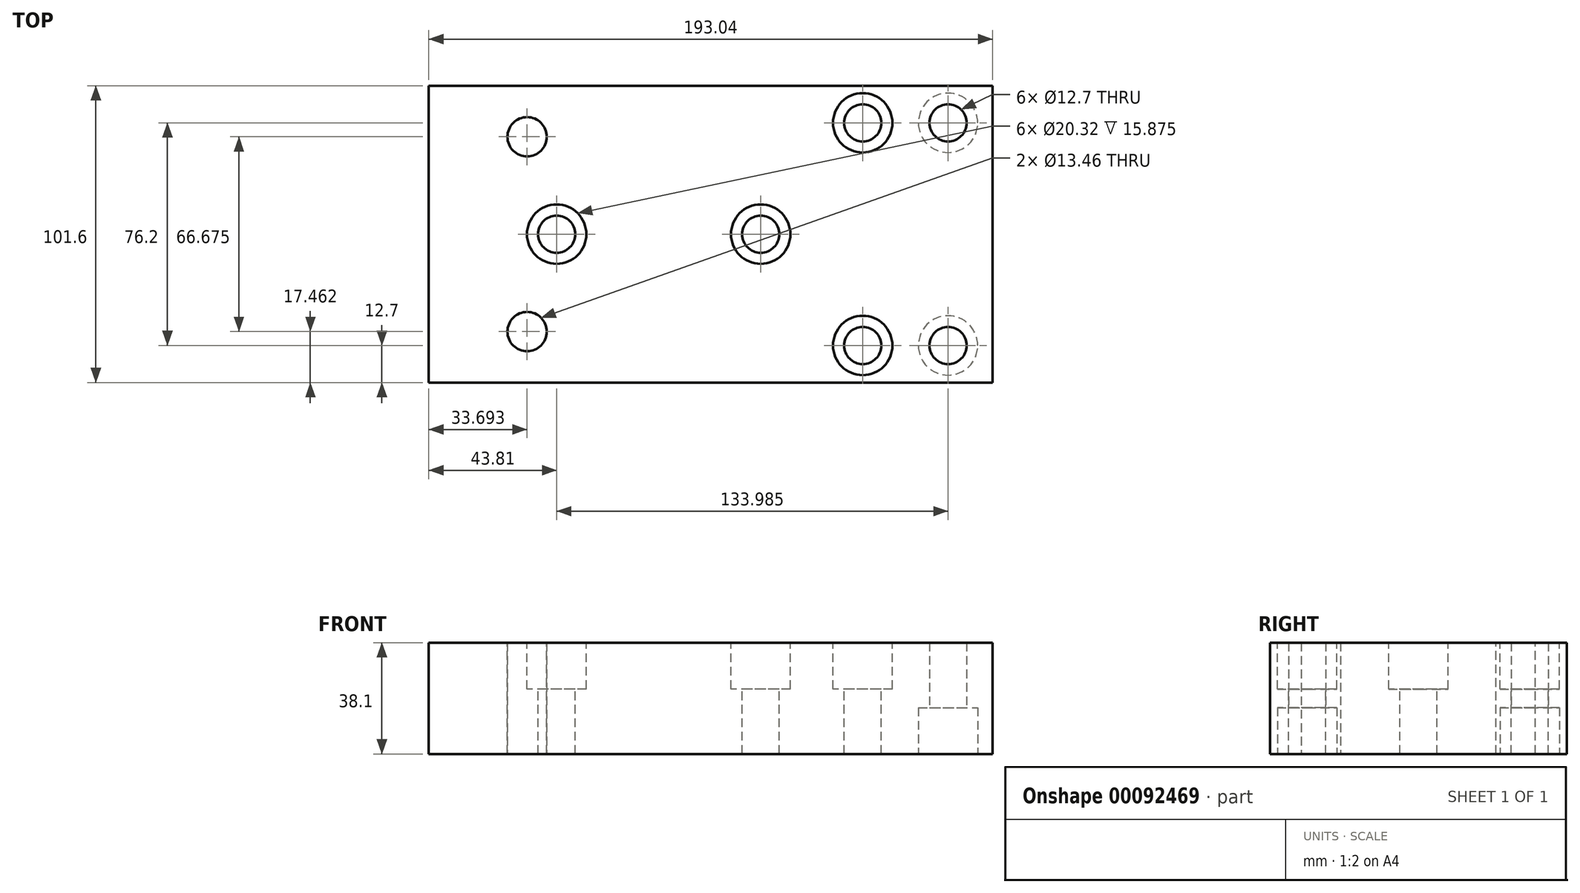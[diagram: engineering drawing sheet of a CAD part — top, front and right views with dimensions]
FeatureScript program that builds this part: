
annotation { "Feature Type Name" : "Feature", "Feature Type Description" : "" }
export const myFeature = defineFeature(function(context is Context, id is Id, definition is map)
    precondition{}
    {
        {
            var Q0;
            Q0=qCreatedBy(makeId("Top.planeOp"),FACE);
            var sketch = newSketch(context, id + "F0", { "sketchPlane" : qUnion([Q0])});
            skCircle(sketch, "E0", {"center": v(685.93, -42.2) * mm, "radius": 6.73 * mm});
            skCircle(sketch, "E1", {"center": v(685.93, 24.48) * mm, "radius": 6.73 * mm});
            skLineSegment(sketch, "E2", {"start": v(845.28, 41.94) * mm, "end": v(652.24, 41.94) * mm});
            skCircle(sketch, "E3", {"center": v(830.04, -46.96) * mm, "radius": 6.53 * mm});
            skCircle(sketch, "E4", {"center": v(830.04, 29.24) * mm, "radius": 6.53 * mm});
            skLineSegment(sketch, "E5", {"start": v(652.24, -59.66) * mm, "end": v(652.24, 41.94) * mm});
            skCircle(sketch, "E6", {"center": v(800.83, 29.24) * mm, "radius": 6.35 * mm});
            skCircle(sketch, "E7", {"center": v(800.83, -46.96) * mm, "radius": 6.35 * mm});
            skCircle(sketch, "E8", {"center": v(696.05, -8.86) * mm, "radius": 6.35 * mm});
            skCircle(sketch, "E9", {"center": v(765.9, -8.86) * mm, "radius": 6.35 * mm});
            skCircle(sketch, "E10", {"center": v(696.05, -8.86) * mm, "radius": 10.16 * mm});
            skCircle(sketch, "E11", {"center": v(765.9, -8.86) * mm, "radius": 10.16 * mm});
            skCircle(sketch, "E12", {"center": v(800.83, 29.24) * mm, "radius": 10.16 * mm});
            skCircle(sketch, "E13", {"center": v(800.83, -46.96) * mm, "radius": 10.16 * mm});
            skCircle(sketch, "E14", {"center": v(830.04, 29.24) * mm, "radius": 10.16 * mm});
            skCircle(sketch, "E15", {"center": v(830.04, -46.96) * mm, "radius": 10.16 * mm});
            skCircle(sketch, "E16", {"center": v(685.93, -191.42) * mm, "radius": 6.73 * mm});
            skCircle(sketch, "E17", {"center": v(685.93, -258.1) * mm, "radius": 6.73 * mm});
            skLineSegment(sketch, "E18", {"start": v(845.28, -97.76) * mm, "end": v(845.28, -135.86) * mm});
            skLineSegment(sketch, "E19", {"start": v(845.28, -275.56) * mm, "end": v(652.24, -275.56) * mm});
            skLineSegment(sketch, "E20", {"start": v(845.28, -173.96) * mm, "end": v(652.24, -173.96) * mm});
            skCircle(sketch, "E21", {"center": v(830.04, -186.66) * mm, "radius": 6.53 * mm});
            skCircle(sketch, "E22", {"center": v(830.04, -262.86) * mm, "radius": 6.53 * mm});
            skCircle(sketch, "E23", {"center": v(800.83, -262.86) * mm, "radius": 6.35 * mm});
            skCircle(sketch, "E24", {"center": v(800.83, -186.66) * mm, "radius": 6.35 * mm});
            skCircle(sketch, "E25", {"center": v(696.05, -224.76) * mm, "radius": 6.35 * mm});
            skCircle(sketch, "E26", {"center": v(765.9, -224.76) * mm, "radius": 6.35 * mm});
            skCircle(sketch, "E27", {"center": v(800.83, -262.86) * mm, "radius": 10.16 * mm});
            skCircle(sketch, "E28", {"center": v(800.83, -186.66) * mm, "radius": 10.16 * mm});
            skCircle(sketch, "E29", {"center": v(765.9, -224.76) * mm, "radius": 10.16 * mm});
            skCircle(sketch, "E30", {"center": v(696.05, -224.76) * mm, "radius": 10.16 * mm});
            skCircle(sketch, "E31", {"center": v(830.04, -186.66) * mm, "radius": 10.16 * mm});
            skCircle(sketch, "E32", {"center": v(830.04, -262.86) * mm, "radius": 10.16 * mm});
            skLineSegment(sketch, "E33", {"start": v(845.28, -173.96) * mm, "end": v(845.28, -275.56) * mm});
            skLineSegment(sketch, "E34", {"start": v(652.24, -97.76) * mm, "end": v(845.28, -97.76) * mm});
            skLineSegment(sketch, "E35", {"start": v(692.66, -97.76) * mm, "end": v(692.66, -135.86) * mm});
            skLineSegment(sketch, "E36", {"start": v(836.64, -97.76) * mm, "end": v(836.64, -121.57) * mm});
            skLineSegment(sketch, "E37", {"start": v(823.43, -121.57) * mm, "end": v(823.43, -97.76) * mm});
            skLineSegment(sketch, "E38", {"start": v(819.88, -135.86) * mm, "end": v(819.88, -121.57) * mm});
            skLineSegment(sketch, "E39", {"start": v(840.2, -121.57) * mm, "end": v(840.2, -135.86) * mm});
            skLineSegment(sketch, "E40", {"start": v(819.88, -121.57) * mm, "end": v(823.43, -121.57) * mm});
            skLineSegment(sketch, "E41", {"start": v(823.43, -121.57) * mm, "end": v(830.04, -121.57) * mm});
            skLineSegment(sketch, "E42", {"start": v(830.04, -121.57) * mm, "end": v(836.64, -121.57) * mm});
            skLineSegment(sketch, "E43", {"start": v(836.64, -121.57) * mm, "end": v(840.2, -121.57) * mm});
            skLineSegment(sketch, "E44", {"start": v(679.2, -97.76) * mm, "end": v(679.2, -135.86) * mm});
            skLineSegment(sketch, "E45", {"start": v(790.67, -112.05) * mm, "end": v(790.67, -97.76) * mm});
            skLineSegment(sketch, "E46", {"start": v(790.67, -112.05) * mm, "end": v(810.99, -112.05) * mm});
            skLineSegment(sketch, "E47", {"start": v(794.48, -135.86) * mm, "end": v(794.48, -112.05) * mm});
            skLineSegment(sketch, "E48", {"start": v(807.18, -112.05) * mm, "end": v(807.18, -135.86) * mm});
            skLineSegment(sketch, "E49", {"start": v(810.99, -97.76) * mm, "end": v(810.99, -112.05) * mm});
            skLineSegment(sketch, "E50", {"start": v(755.74, -112.05) * mm, "end": v(755.74, -97.76) * mm});
            skLineSegment(sketch, "E51", {"start": v(755.74, -112.05) * mm, "end": v(776.06, -112.05) * mm});
            skLineSegment(sketch, "E52", {"start": v(759.55, -135.86) * mm, "end": v(759.55, -112.05) * mm});
            skLineSegment(sketch, "E53", {"start": v(772.25, -112.05) * mm, "end": v(772.25, -135.86) * mm});
            skLineSegment(sketch, "E54", {"start": v(776.06, -97.76) * mm, "end": v(776.06, -112.05) * mm});
            skLineSegment(sketch, "E55", {"start": v(759.55, -173.96) * mm, "end": v(772.25, -173.96) * mm});
            skLineSegment(sketch, "E56", {"start": v(685.9, -112.05) * mm, "end": v(685.9, -97.76) * mm});
            skLineSegment(sketch, "E57", {"start": v(685.9, -112.05) * mm, "end": v(706.21, -112.05) * mm});
            skLineSegment(sketch, "E58", {"start": v(689.7, -135.86) * mm, "end": v(689.7, -112.05) * mm});
            skLineSegment(sketch, "E59", {"start": v(702.4, -112.05) * mm, "end": v(702.4, -135.86) * mm});
            skLineSegment(sketch, "E60", {"start": v(706.21, -97.76) * mm, "end": v(706.21, -112.05) * mm});
            skLineSegment(sketch, "E61", {"start": v(689.7, -173.96) * mm, "end": v(702.4, -173.96) * mm});
            skLineSegment(sketch, "E62", {"start": v(652.24, -135.86) * mm, "end": v(845.28, -135.86) * mm});
            skLineSegment(sketch, "E63", {"start": v(652.24, -59.66) * mm, "end": v(845.28, -59.66) * mm});
            skLineSegment(sketch, "E64", {"start": v(845.28, -59.66) * mm, "end": v(845.28, 41.94) * mm});
            skLineSegment(sketch, "E65", {"start": v(652.24, -135.86) * mm, "end": v(652.24, -97.76) * mm});
            skLineSegment(sketch, "E66", {"start": v(652.24, -275.56) * mm, "end": v(652.24, -173.96) * mm});
            skSolve(sketch);
        }
        {
            var Q0;
            Q0=makeQuery(id+"F0.imprint","IMPRINT",FACE,{"disambiguationData":[TD([[makeQuery(id+"F0.imprint","IMPRINT",EDGE,{"derivedFrom":sQuery(id+"F0.wireOp",EDGE,"E6")}),-1.0]])]});
            var Q1;
            Q1=makeQuery(id+"F0.imprint","IMPRINT",FACE,{"disambiguationData":[TD([[makeQuery(id+"F0.imprint","IMPRINT",EDGE,{"derivedFrom":sQuery(id+"F0.wireOp",EDGE,"E9")}),-1.0]])]});
            var Q2;
            Q2=makeQuery(id+"F0.imprint","IMPRINT",FACE,{"disambiguationData":[TD([[makeQuery(id+"F0.imprint","IMPRINT",EDGE,{"derivedFrom":sQuery(id+"F0.wireOp",EDGE,"E3")}),1.0]])]});
            var Q3;
            Q3=makeQuery(id+"F0.imprint","IMPRINT",FACE,{"disambiguationData":[TD([[makeQuery(id+"F0.imprint","IMPRINT",EDGE,{"derivedFrom":sQuery(id+"F0.wireOp",EDGE,"E6")}),1.0]])]});
            var Q4;
            Q4=makeQuery(id+"F0.imprint","IMPRINT",FACE,{"disambiguationData":[TD([[makeQuery(id+"F0.imprint","IMPRINT",EDGE,{"derivedFrom":sQuery(id+"F0.wireOp",EDGE,"E4")}),1.0]])]});
            var Q5;
            Q5=makeQuery(id+"F0.imprint","IMPRINT",FACE,{"disambiguationData":[TD([[makeQuery(id+"F0.imprint","IMPRINT",EDGE,{"derivedFrom":sQuery(id+"F0.wireOp",EDGE,"E8")}),1.0]])]});
            var Q6;
            Q6=makeQuery(id+"F0.imprint","IMPRINT",FACE,{"disambiguationData":[TD([[makeQuery(id+"F0.imprint","IMPRINT",EDGE,{"derivedFrom":sQuery(id+"F0.wireOp",EDGE,"E1")}),-1.0]])]});
            var Q7;
            Q7=makeQuery(id+"F0.imprint","IMPRINT",FACE,{"disambiguationData":[TD([[makeQuery(id+"F0.imprint","IMPRINT",EDGE,{"derivedFrom":sQuery(id+"F0.wireOp",EDGE,"E8")}),-1.0]])]});
            var Q8;
            Q8=makeQuery(id+"F0.imprint","IMPRINT",FACE,{"disambiguationData":[TD([[makeQuery(id+"F0.imprint","IMPRINT",EDGE,{"derivedFrom":sQuery(id+"F0.wireOp",EDGE,"E7")}),-1.0]])]});
            var Q9;
            Q9=makeQuery(id+"F0.imprint","IMPRINT",FACE,{"disambiguationData":[TD([[makeQuery(id+"F0.imprint","IMPRINT",EDGE,{"derivedFrom":sQuery(id+"F0.wireOp",EDGE,"E7")}),1.0]])]});
            var Q10;
            Q10=makeQuery(id+"F0.imprint","IMPRINT",FACE,{"disambiguationData":[TD([[makeQuery(id+"F0.imprint","IMPRINT",EDGE,{"derivedFrom":sQuery(id+"F0.wireOp",EDGE,"E9")}),1.0]])]});
            var Q11;
            Q11=makeQuery(id+"F0.imprint","IMPRINT",FACE,{"disambiguationData":[TD([[makeQuery(id+"F0.imprint","IMPRINT",EDGE,{"derivedFrom":sQuery(id+"F0.wireOp",EDGE,"E0")}),-1.0]])]});
            var Q12;
            Q12=makeQuery(id+"F0.imprint","IMPRINT",FACE,{"disambiguationData":[TD([[makeQuery(id+"F0.imprint","IMPRINT",EDGE,{"derivedFrom":sQuery(id+"F0.wireOp",EDGE,"E0")}),1.0]])]});
            var Q13;
            Q13=makeQuery(id+"F0.imprint","IMPRINT",FACE,{"disambiguationData":[TD([[makeQuery(id+"F0.imprint","IMPRINT",EDGE,{"derivedFrom":sQuery(id+"F0.wireOp",EDGE,"E3")}),-1.0]])]});
            var Q14;
            Q14=makeQuery(id+"F0.imprint","IMPRINT",FACE,{"disambiguationData":[TD([[makeQuery(id+"F0.imprint","IMPRINT",EDGE,{"derivedFrom":sQuery(id+"F0.wireOp",EDGE,"E4")}),-1.0]])]});
            extrude(context, id + "F1", {"entities" : qUnion([Q0, Q1, Q2, Q3, Q4, Q5, Q6, Q7, Q8, Q9, Q10, Q11, Q12, Q13, Q14]), "oppositeDirection" : true, "depth" : 38.1 * mm});
        }
        {
            var Q0;
            Q0=sQuery(id+"F0.wireOp",VERTEX,"E6.center");
            var Q1;
            Q1=sQuery(id+"F0.wireOp",VERTEX,"E7.center");
            var Q2;
            Q2=sQuery(id+"F0.wireOp",VERTEX,"E9.center");
            var Q3;
            Q3=sQuery(id+"F0.wireOp",VERTEX,"E8.center");
            var Q4;
            Q4=makeQuery(id+"F1.opExtrude","SWEPT_BODY",BODY,{"disambiguationData":[OSD([sQuery(id+"F0.wireOp",EDGE,"E2"),sQuery(id+"F0.wireOp",EDGE,"E5"),sQuery(id+"F0.wireOp",EDGE,"E63"),sQuery(id+"F0.wireOp",EDGE,"E64")])]});
            hole(context, id + "F2", {"style" : HoleStyle.C_BORE, "endStyle" : HoleEndStyle.BLIND, "holeDiameter" : 12.7 * mm, "cBoreDiameter" : 20.32 * mm, "cBoreDepth" : 15.88 * mm, "holeDepth" : 50.8 * mm, "startFromSketch" : true, "locations" : qUnion([Q0, Q1, Q2, Q3]), "scope" : qUnion([Q4])});
        }
        {
            var Q0;
            Q0=makeQuery(id+"F1.opExtrude","SWEPT_BODY",BODY,{"disambiguationData":[OSD([sQuery(id+"F0.wireOp",EDGE,"E2"),sQuery(id+"F0.wireOp",EDGE,"E5"),sQuery(id+"F0.wireOp",EDGE,"E63"),sQuery(id+"F0.wireOp",EDGE,"E64")])]});
            transform(context, id + "F3", {"entities" : qUnion([Q0]), "transformType" : TransformType.TRANSLATION_3D, "dx" : 0 * mm, "dy" : 0 * mm, "dz" : 38.1 * mm, "makeCopy" : false});
        }
        {
            var Q0;
            Q0=sQuery(id+"F0.wireOp",VERTEX,"E1.center");
            var Q1;
            Q1=sQuery(id+"F0.wireOp",VERTEX,"E0.center");
            var Q2;
            Q2=makeQuery(id+"F1.opExtrude","SWEPT_BODY",BODY,{"disambiguationData":[OSD([sQuery(id+"F0.wireOp",EDGE,"E2"),sQuery(id+"F0.wireOp",EDGE,"E5"),sQuery(id+"F0.wireOp",EDGE,"E63"),sQuery(id+"F0.wireOp",EDGE,"E64")])]});
            hole(context, id + "F4", {"style" : HoleStyle.SIMPLE, "endStyle" : HoleEndStyle.BLIND, "oppositeDirection" : true, "holeDiameter" : 13.46 * mm, "holeDepth" : 50.8 * mm, "startFromSketch" : true, "locations" : qUnion([Q0, Q1]), "scope" : qUnion([Q2])});
        }
        {
            var Q0;
            Q0=sQuery(id+"F0.wireOp",VERTEX,"E3.center");
            var Q1;
            Q1=sQuery(id+"F0.wireOp",VERTEX,"E4.center");
            var Q2;
            Q2=makeQuery(id+"F1.opExtrude","SWEPT_BODY",BODY,{"disambiguationData":[OSD([sQuery(id+"F0.wireOp",EDGE,"E2"),sQuery(id+"F0.wireOp",EDGE,"E5"),sQuery(id+"F0.wireOp",EDGE,"E63"),sQuery(id+"F0.wireOp",EDGE,"E64")])]});
            hole(context, id + "F5", {"style" : HoleStyle.C_BORE, "endStyle" : HoleEndStyle.BLIND, "oppositeDirection" : true, "holeDiameter" : 12.7 * mm, "cBoreDiameter" : 20.32 * mm, "cBoreDepth" : 15.88 * mm, "holeDepth" : 50.8 * mm, "startFromSketch" : true, "locations" : qUnion([Q0, Q1]), "scope" : qUnion([Q2])});
        }
    });
